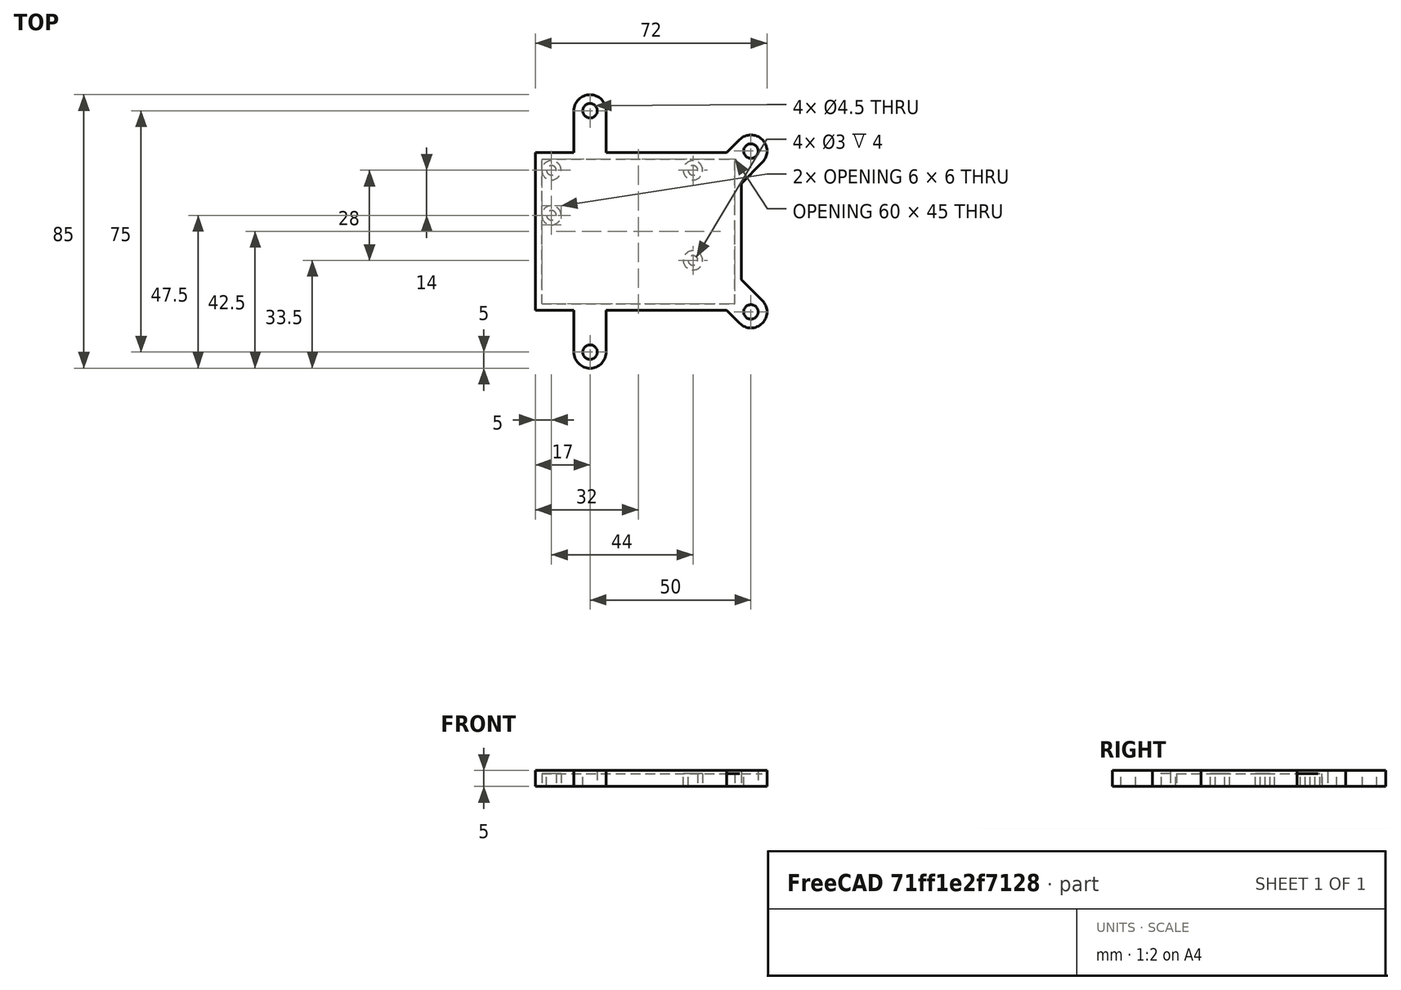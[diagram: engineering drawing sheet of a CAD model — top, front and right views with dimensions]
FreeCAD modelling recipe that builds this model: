
FCSTD DOCUMENT  (FreeCAD 1.0R38641 +678 (Git))
Label: foundation
License: All rights reserved
LicenseURL: https://en.wikipedia.org/wiki/All_rights_reserved
objects: Sketcher::SketchObject×4, PartDesign::Pad×3, PartDesign::Pocket×1, PartDesign::Body×1
note: 21 computed .brp shape members not serialized (recipe doc carries the construction recipe); baked Part::Feature solids carry a one-line shape summary decoded from their .brp

FEATURE [Sketcher::SketchObject] Sketch123
  ArcFitTolerance = 0
  AttachmentSupport = -> [XY_Plane015]
  FullyConstrained = true
  MakeInternals = false
  MapMode = 5
  sketch-geometry (32):
    g0: LineSegment StartX=-30 StartY=22.5 StartZ=0 EndX=30 EndY=22.5 EndZ=0
    g1: LineSegment StartX=-30 StartY=22.5 StartZ=0 EndX=-30 EndY=-22.5 EndZ=0
    g2: LineSegment StartX=-30 StartY=-22.5 StartZ=0 EndX=30 EndY=-22.5 EndZ=0
    g3: LineSegment StartX=30 StartY=22.5 StartZ=0 EndX=30 EndY=-22.5 EndZ=0
    g4: LineSegment StartX=-32 StartY=24.5 StartZ=0 EndX=-20 EndY=24.5 EndZ=0
    g5: LineSegment StartX=27.4289 StartY=-24.5 StartZ=0 EndX=-10 EndY=-24.5 EndZ=0
    g6: LineSegment StartX=-32 StartY=-24.5 StartZ=0 EndX=-32 EndY=24.5 EndZ=0
    g7: GeomPoint [constr] X=35 Y=25 Z=0
    g8: GeomPoint [constr] X=35 Y=-25 Z=0
    g9: GeomPoint [constr] X=-15 Y=-25 Z=0
    g10: GeomPoint [constr] X=-15 Y=25 Z=0
    g11: GeomPoint [constr] X=-15 Y=-37.5 Z=0
    g12: GeomPoint [constr] X=-15 Y=37.5 Z=0
    g13: ArcOfCircle CenterX=35 CenterY=-25 CenterZ=0 NormalX=0 NormalY=0 NormalZ=1 AngleXU=0 Radius=5 StartAngle=3.92699 EndAngle=7.06858
    g14: ArcOfCircle CenterX=35 CenterY=25 CenterZ=0 NormalX=0 NormalY=0 NormalZ=1 AngleXU=0 Radius=5 StartAngle=5.49779 EndAngle=8.63938
    g15: ArcOfCircle CenterX=-15 CenterY=37.5 CenterZ=0 NormalX=0 NormalY=0 NormalZ=1 AngleXU=0 Radius=5 StartAngle=0 EndAngle=3.14159
    g16: ArcOfCircle CenterX=-15 CenterY=-37.5 CenterZ=0 NormalX=0 NormalY=0 NormalZ=1 AngleXU=0 Radius=5 StartAngle=3.14159 EndAngle=6.28319
    g17: LineSegment StartX=27.4289 StartY=24.5 StartZ=0 EndX=31.4645 EndY=28.5355 EndZ=0
    g18: LineSegment StartX=32 StartY=14.9289 StartZ=0 EndX=38.5355 EndY=21.4645 EndZ=0
    g19: LineSegment StartX=-20 StartY=24.5 StartZ=0 EndX=-20 EndY=37.5 EndZ=0
    g20: LineSegment StartX=-10 StartY=24.5 StartZ=0 EndX=-10 EndY=37.5 EndZ=0
    g21: LineSegment StartX=-20 StartY=-24.5 StartZ=0 EndX=-20 EndY=-37.5 EndZ=0
    g22: LineSegment StartX=-10 StartY=-24.5 StartZ=0 EndX=-10 EndY=-37.5 EndZ=0
    g23: LineSegment StartX=27.4289 StartY=-24.5 StartZ=0 EndX=31.4645 EndY=-28.5355 EndZ=0
    g24: LineSegment StartX=32 StartY=-14.9289 StartZ=0 EndX=38.5355 EndY=-21.4645 EndZ=0
    g25: GeomPoint [constr] X=30 Y=20 Z=0
    g26: LineSegment [constr] StartX=30 StartY=20 StartZ=0 EndX=35 EndY=25 EndZ=0
    g27: GeomPoint [constr] X=30 Y=-20 Z=0
    g28: LineSegment [constr] StartX=30 StartY=-20 StartZ=0 EndX=35 EndY=-25 EndZ=0
    g29: LineSegment StartX=-20 StartY=-24.5 StartZ=0 EndX=-32 EndY=-24.5 EndZ=0
    g30: LineSegment StartX=-10 StartY=24.5 StartZ=0 EndX=27.4289 EndY=24.5 EndZ=0
    g31: LineSegment StartX=32 StartY=14.9289 StartZ=0 EndX=32 EndY=-14.9289 EndZ=0
  constraints (78):
    c: Horizontal(g0)
    c: DistanceX(g0,g0) = 60
    c: Coincident(g1,g0)
    c: Vertical(g1)
    c: DistanceY(g1,g1) = 45
    c: Distance(g-1,g0) = 22.5
    c: Distance(g-1,g1) = 30
    c: Coincident(g2,g1)
    c: Horizontal(g2)
    c: Coincident(g3,g0)
    c: Coincident(g3,g2)
    c: Vertical(g3)
    c: Horizontal(g4)
    c: Horizontal(g5)
    c: Coincident(g6,g29)
    c: Coincident(g6,g4)
    c: Vertical(g6)
    c: Distance(g0,g4) = 2
    c: DistanceY(g-1,g8) = -25
    c: DistanceY(g-1,g10) = 25
    c: DistanceY(g-1,g7) = 25
    c: DistanceY(g-1,g9) = -25
    c: Distance(g9,g8) = 50
    c: Distance(g10,g7) = 50
    c: DistanceX(g-2,g9) = -15
    c: DistanceX(g-2,g10) = -15
    c: Distance(g11,g9) = 12.5
    c: DistanceX(g-2,g11) = -15
    c: Distance(g12,g10) = 12.5
    c: DistanceX(g-2,g12) = -15
    c: Coincident(g13,g8)
    c: Coincident(g14,g7)
    c: Coincident(g15,g12)
    c: Coincident(g16,g11)
    c: Diameter(g14) = 10
    c: Equal(g14,g15)
    c: Equal(g15,g16)
    c: Equal(g16,g13)
    c: PointOnObject(g17,g4)
    c: Vertical(g19)
    c: Vertical(g20)
    c: Vertical(g21)
    c: Vertical(g22)
    c: PointOnObject(g25,g3)
    c: Distance(g25,g0) = 2.5
    c: Coincident(g26,g25)
    c: Coincident(g26,g14)
    c: Parallel(g26,g18)
    c: Parallel(g26,g17)
    c: PointOnObject(g27,g3)
    c: Distance(g27,g2) = 2.5
    c: Coincident(g28,g27)
    c: Coincident(g28,g13)
    c: Parallel(g28,g24)
    c: Parallel(g28,g23)
    c: Coincident(g5,g22)
    c: Coincident(g29,g21)
    c: Coincident(g4,g19)
    c: Coincident(g30,g20)
    c: Coincident(g31,g18)
    c: Tangent(g15,g19) = 1.5708
    c: Tangent(g15,g20) = -1.5708
    c: Tangent(g14,g18) = -1.5708
    c: Tangent(g14,g17) = 1.5708
    c: Tangent(g13,g24) = 1.5708
    c: Coincident(g5,g23)
    c: Tangent(g13,g23) = -1.5708
    c: Tangent(g16,g22) = 1.5708
    c: Tangent(g16,g21) = -1.5708
    c: Distance(g18,g3) = 2
    c: Distance(g5,g2) = 2
    c: Distance(g6,g2) = 2
    c: Distance(g6,g1) = 2
    c: Coincident(g31,g24)
    c: Vertical(g31)
    c: Horizontal(g29)
    c: Coincident(g30,g17)
    c: Horizontal(g30)
FEATURE [PartDesign::Pad] Pad050
  Direction = (0,0,1)
  Length = 5
  Length2 = 10
  Profile = -> Sketch123
  ReferenceAxis = -> Sketch123 [N_Axis]
  Suppressed = false
  Type = 0
FEATURE [Sketcher::SketchObject] Sketch128
  ArcFitTolerance = 0
  FullyConstrained = true
  MakeInternals = false
  MapMode = 5
  sketch-geometry (8):
    g0: Circle CenterX=-27 CenterY=-5 CenterZ=0 NormalX=0 NormalY=0 NormalZ=1 AngleXU=0 Radius=1.5
    g1: Circle CenterX=17 CenterY=9 CenterZ=0 NormalX=0 NormalY=0 NormalZ=1 AngleXU=0 Radius=1.5
    g2: Circle CenterX=17 CenterY=-19 CenterZ=0 NormalX=0 NormalY=0 NormalZ=1 AngleXU=0 Radius=1.5
    g3: Circle CenterX=-27 CenterY=-19 CenterZ=0 NormalX=0 NormalY=0 NormalZ=1 AngleXU=0 Radius=1.5
    g4: Circle CenterX=-27 CenterY=-5 CenterZ=0 NormalX=0 NormalY=0 NormalZ=1 AngleXU=0 Radius=3
    g5: Circle CenterX=-27 CenterY=-19 CenterZ=0 NormalX=0 NormalY=0 NormalZ=1 AngleXU=0 Radius=3
    g6: Circle CenterX=17 CenterY=9 CenterZ=0 NormalX=0 NormalY=0 NormalZ=1 AngleXU=0 Radius=3
    g7: Circle CenterX=17 CenterY=-19 CenterZ=0 NormalX=0 NormalY=0 NormalZ=1 AngleXU=0 Radius=3
  constraints (20):
    c: Diameter(g0) = 3
    c: Equal(g1,g0)
    c: Equal(g2,g1)
    c: Distance(g2,g1) = 28
    c: Equal(g3,g1)
    c: Distance(g3,g0) = 14
    c: Coincident(g4,g0)
    c: Diameter(g4) = 6
    c: Coincident(g5,g3)
    c: Coincident(g6,g1)
    c: Coincident(g7,g2)
    c: Equal(g7,g5)
    c: Equal(g5,g6)
    c: Equal(g6,g4)
    c: DistanceX(g-2,g2) = 17
    c: DistanceX(g-2,g3) = -27
    c: DistanceX(g-2,g0) = -27
    c: DistanceX(g-2,g1) = 17
    c: DistanceY(g-1,g3) = -19
    c: DistanceY(g-1,g2) = -19
FEATURE [Sketcher::SketchObject] Sketch222
  ArcFitTolerance = 0
  AttachmentSupport = -> [XY_Plane015]
  FullyConstrained = true
  MakeInternals = false
  MapMode = 5
  sketch-geometry (28):
    g0: LineSegment StartX=-31 StartY=23.5 StartZ=0 EndX=-20 EndY=23.5 EndZ=0
    g1: LineSegment StartX=26.43 StartY=-23.5 StartZ=0 EndX=-10 EndY=-23.5 EndZ=0
    g2: LineSegment StartX=-31 StartY=-23.5 StartZ=0 EndX=-31 EndY=23.5 EndZ=0
    g3: GeomPoint [constr] X=35 Y=25 Z=0
    g4: GeomPoint [constr] X=35 Y=-25 Z=0
    g5: GeomPoint [constr] X=-15 Y=-25 Z=0
    g6: GeomPoint [constr] X=-15 Y=25 Z=0
    g7: GeomPoint [constr] X=-15 Y=-37.5 Z=0
    g8: GeomPoint [constr] X=-15 Y=37.5 Z=0
    g9: ArcOfCircle CenterX=35 CenterY=-25 CenterZ=0 NormalX=0 NormalY=0 NormalZ=1 AngleXU=0 Radius=5 StartAngle=3.92688 EndAngle=7.06848
    g10: ArcOfCircle CenterX=35 CenterY=25 CenterZ=0 NormalX=0 NormalY=0 NormalZ=1 AngleXU=0 Radius=5 StartAngle=5.49754 EndAngle=8.63913
    g11: ArcOfCircle CenterX=-15 CenterY=37.5 CenterZ=0 NormalX=0 NormalY=0 NormalZ=1 AngleXU=0 Radius=5 StartAngle=0 EndAngle=3.14159
    g12: ArcOfCircle CenterX=-15 CenterY=-37.5 CenterZ=0 NormalX=0 NormalY=0 NormalZ=1 AngleXU=0 Radius=5 StartAngle=3.14159 EndAngle=6.28319
    g13: LineSegment StartX=26.4264 StartY=23.5 StartZ=0 EndX=31.4653 EndY=28.5364 EndZ=0
    g14: LineSegment StartX=31 StartY=13.9327 StartZ=0 EndX=38.5347 EndY=21.4636 EndZ=0
    g15: LineSegment StartX=-20 StartY=23.5 StartZ=0 EndX=-20 EndY=37.5 EndZ=0
    g16: LineSegment StartX=-10 StartY=23.5 StartZ=0 EndX=-10 EndY=37.5 EndZ=0
    g17: LineSegment StartX=-20 StartY=-23.5 StartZ=0 EndX=-20 EndY=-37.5 EndZ=0
    g18: LineSegment StartX=-10 StartY=-23.5 StartZ=0 EndX=-10 EndY=-37.5 EndZ=0
    g19: LineSegment StartX=26.43 StartY=-23.5 StartZ=0 EndX=31.4641 EndY=-28.5352 EndZ=0
    g20: LineSegment StartX=31 StartY=-13.9273 StartZ=0 EndX=38.5359 EndY=-21.4648 EndZ=0
    g21: GeomPoint [constr] X=29.9975 Y=20 Z=0
    g22: LineSegment [constr] StartX=29.9975 StartY=20 StartZ=0 EndX=35 EndY=25 EndZ=0
    g23: GeomPoint [constr] X=30.0011 Y=-20 Z=0
    g24: LineSegment [constr] StartX=30.0011 StartY=-20 StartZ=0 EndX=35 EndY=-25 EndZ=0
    g25: LineSegment StartX=-20 StartY=-23.5 StartZ=0 EndX=-31 EndY=-23.5 EndZ=0
    g26: LineSegment StartX=-10 StartY=23.5 StartZ=0 EndX=26.4264 EndY=23.5 EndZ=0
    g27: LineSegment StartX=31 StartY=13.9327 StartZ=0 EndX=31 EndY=-13.9273 EndZ=0
  constraints (66):
    c: Horizontal(g0)
    c: Horizontal(g1)
    c: Coincident(g2,g25)
    c: Coincident(g2,g0)
    c: Vertical(g2)
    c: DistanceY(g-1,g4) = -25
    c: DistanceY(g-1,g6) = 25
    c: DistanceY(g-1,g3) = 25
    c: DistanceY(g-1,g5) = -25
    c: Distance(g5,g4) = 50
    c: Distance(g6,g3) = 50
    c: DistanceX(g-2,g5) = -15
    c: DistanceX(g-2,g6) = -15
    c: Distance(g7,g5) = 12.5
    c: DistanceX(g-2,g7) = -15
    c: Distance(g8,g6) = 12.5
    c: DistanceX(g-2,g8) = -15
    c: Coincident(g9,g4)
    c: Coincident(g10,g3)
    c: Coincident(g11,g8)
    c: Coincident(g12,g7)
    c: Diameter(g10) = 10
    c: Equal(g10,g11)
    c: Equal(g11,g12)
    c: Equal(g12,g9)
    c: PointOnObject(g13,g0)
    c: Vertical(g15)
    c: Vertical(g16)
    c: Vertical(g17)
    c: Vertical(g18)
    c: Coincident(g22,g21)
    c: Coincident(g22,g10)
    c: Parallel(g22,g14)
    c: Parallel(g22,g13)
    c: Coincident(g24,g23)
    c: Coincident(g24,g9)
    c: Parallel(g24,g20)
    c: Parallel(g24,g19)
    c: Coincident(g1,g18)
    c: Coincident(g25,g17)
    c: Coincident(g0,g15)
    c: Coincident(g26,g16)
    c: Coincident(g27,g14)
    c: Tangent(g11,g15) = 1.5708
    c: Tangent(g11,g16) = -1.5708
    c: Tangent(g10,g14) = -1.5708
    c: Tangent(g10,g13) = 1.5708
    c: Tangent(g9,g20) = 1.5708
    c: Coincident(g1,g19)
    c: Tangent(g9,g19) = -1.5708
    c: Tangent(g12,g18) = 1.5708
    c: Tangent(g12,g17) = -1.5708
    c: Coincident(g27,g20)
    c: Vertical(g27)
    c: Horizontal(g25)
    c: Coincident(g26,g13)
    c: Horizontal(g26)
    c: Distance(g-1,g2) = 31
    c: Distance(g-1,g27) = 31
    c: Distance(g-1,g1) = 23.5
    c: Distance(g-1,g26) = 23.5
    c: DistanceY(g2,g2) = 47
    c: DistanceY(g27,g27) = 27.86
    c: DistanceX(g1,g1) = 36.43
    c: DistanceY(g-1,g21) = 20
    c: DistanceY(g-1,g23) = -20
FEATURE [PartDesign::Pad] Pad099
  BaseFeature = -> Pad050
  Direction = (0,0,1)
  Length = 1
  Length2 = 10
  Profile = -> Sketch222
  ReferenceAxis = -> Sketch222 [N_Axis]
  Suppressed = false
  Type = 0
FEATURE [PartDesign::Pad] Pad100
  BaseFeature = -> Pad099
  Direction = (0,0,1)
  Length = 5
  Length2 = 10
  Profile = -> Sketch128
  ReferenceAxis = -> Sketch128 [N_Axis]
  Suppressed = false
  Type = 0
FEATURE [Sketcher::SketchObject] Sketch223
  ArcFitTolerance = 0
  AttachmentSupport = -> [XY_Plane015]
  FullyConstrained = true
  MakeInternals = false
  MapMode = 5
  sketch-geometry (10):
    g0: GeomPoint [constr] X=35 Y=25 Z=0
    g1: GeomPoint [constr] X=35 Y=-25 Z=0
    g2: GeomPoint [constr] X=-15 Y=-25 Z=0
    g3: GeomPoint [constr] X=-15 Y=25 Z=0
    g4: GeomPoint [constr] X=-15 Y=-37.5 Z=0
    g5: GeomPoint [constr] X=-15 Y=37.5 Z=0
    g6: Circle CenterX=35 CenterY=-25 CenterZ=0 NormalX=0 NormalY=0 NormalZ=1 AngleXU=0 Radius=2.25
    g7: Circle CenterX=35 CenterY=25 CenterZ=0 NormalX=0 NormalY=0 NormalZ=1 AngleXU=0 Radius=2.25
    g8: Circle CenterX=-15 CenterY=37.5 CenterZ=0 NormalX=0 NormalY=0 NormalZ=1 AngleXU=0 Radius=2.25
    g9: Circle CenterX=-15 CenterY=-37.5 CenterZ=0 NormalX=0 NormalY=0 NormalZ=1 AngleXU=0 Radius=2.25
  constraints (20):
    c: DistanceY(g-1,g1) = -25
    c: DistanceY(g-1,g3) = 25
    c: DistanceY(g-1,g0) = 25
    c: DistanceY(g-1,g2) = -25
    c: Distance(g2,g1) = 50
    c: Distance(g3,g0) = 50
    c: DistanceX(g-2,g2) = -15
    c: DistanceX(g-2,g3) = -15
    c: Distance(g4,g2) = 12.5
    c: DistanceX(g-2,g4) = -15
    c: Distance(g5,g3) = 12.5
    c: DistanceX(g-2,g5) = -15
    c: Coincident(g6,g1)
    c: Coincident(g7,g0)
    c: Coincident(g8,g5)
    c: Coincident(g9,g4)
    c: Diameter(g7) = 4.5
    c: Equal(g7,g8)
    c: Equal(g8,g6)
    c: Equal(g6,g9)
FEATURE [PartDesign::Pocket] Pocket090
  BaseFeature = -> Pad100
  Direction = (0,0,-1)
  Length = 5
  Length2 = 5
  Profile = -> Sketch223
  ReferenceAxis = -> Sketch223 [N_Axis]
  Reversed = true
  Suppressed = false
  Type = 0
FEATURE [PartDesign::Body] Body015  label="foundation"
  AllowCompound = false
  Group = -> [Sketch123,Pad050,Sketch222,Pad099,Sketch128,Pad100,Sketch223,Pocket090]
  Origin = -> Origin015
  Placement = pos=(-216,-3.2e-14,33) rot=(1,0,0;3.14159rad)
  Tip = -> Pocket090
